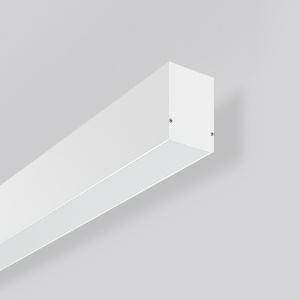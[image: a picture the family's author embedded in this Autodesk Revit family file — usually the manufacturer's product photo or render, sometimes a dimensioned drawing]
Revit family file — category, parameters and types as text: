
# Revit family: less_is_more_50_312612_002_1_84d0
name_source: partatom
category: Lighting Fixtures
units: mm (PartAtom-declared; Revit-internal decimal feet)

## family parameters
Cut with Voids When Loaded = No
Host = Face
Light Source = No
Part Type = Normal
Room Calculation Point = No
Round Connector Dimension = Use Diameter
Shared = No

## types (1)
- LESS IS MORE 50 (1 x LED Modul 840, 4100 lm, 4000)
    Apparent Load = 30 VA
    CIE Flux Codes = 48 80 96 50 100
    Color Rendering = 80
    Color Temperature = 4000
    Default Elevation = 1800 mm
    Description = Series: LESS IS MORE 50
Linear wall luminaires. Housing: extruded aluminium profile, powder-coated. End cap aluminium powder-coated. Diffuser made of non-yellowing plastic (PMMA), opal. Direct 50%, indirect 50% light emission. Suitable for Wall (surface). LED unit with integrated converter interchangeable and removable. Suitable for through-wiring. With sensors or as a safety luminaire on request. 
Colour: traffic white, matt (RAL 9016)
Length: 1687 mm
Width: 67 mm
Height: 75 mm
Lamp: LED
Socket: without socket
Colour temperature: 4000K
Colour rendering index (CRI): 80
Light source: LED
Socket lamp2: Without base
Colour temperature: 4000K
Colour rendering index (CRI) 2: 80
System power: 30 W
Rated luminous flux: 4100 lm
Luminous efficiency: 137 lm/W
Control gear: Regulated power supply
Control gear: Regulated power supply
Protection class: I
Type of protection: IP 20
    Height = 75 mm
    Lamp = 1 x LED Modul 840
    Lamp Light Flux = 4100 lm
    Lamp count = 1
    Length = 1687 mm
    Lifetime = 50000 h
    Luminous efficacy = 137 lm/W
    Manufacturer = RZB
    ModVariant = No
    Model = 312612.002.1
    Mounting Place = Wall
    Mounting Type = Surface mounted
    Number of Poles = 1
    OnlyDefault = Yes
    Power Factor = 1
    Product Name = LESS IS MORE 50
    Product group = Surface mounted LED linear luminaires
    ProductGroupID = 2007
    Protection Class = Protection class I
    Protection Degree = IP 20
    RLX_Detail_Level = 1
    RLX_Emergency_Light_Flux = 0 lm
    RLX_Emergency_Type = 0
    RLX_Emergency_Type_DB = No
    RlxData = <blob elided: 39593 chars, md5=2581ffb3>
    Socket = socket
    Standby Power = 0 W
    System Light Flux = 4100 lm
    System Power = 30 W
    Type Comments = Product without accessories
    Type Image = 312606.002.jpg
    URL = http://relux.com
    VarID = ---
    Voltage = 0 V
    Weight = 0.00 kg
    Width = 67 mm

## geometry (parser evidence)
native form markers: Blend x4, Sweep x11
no freeform markers — native parametric forms only
